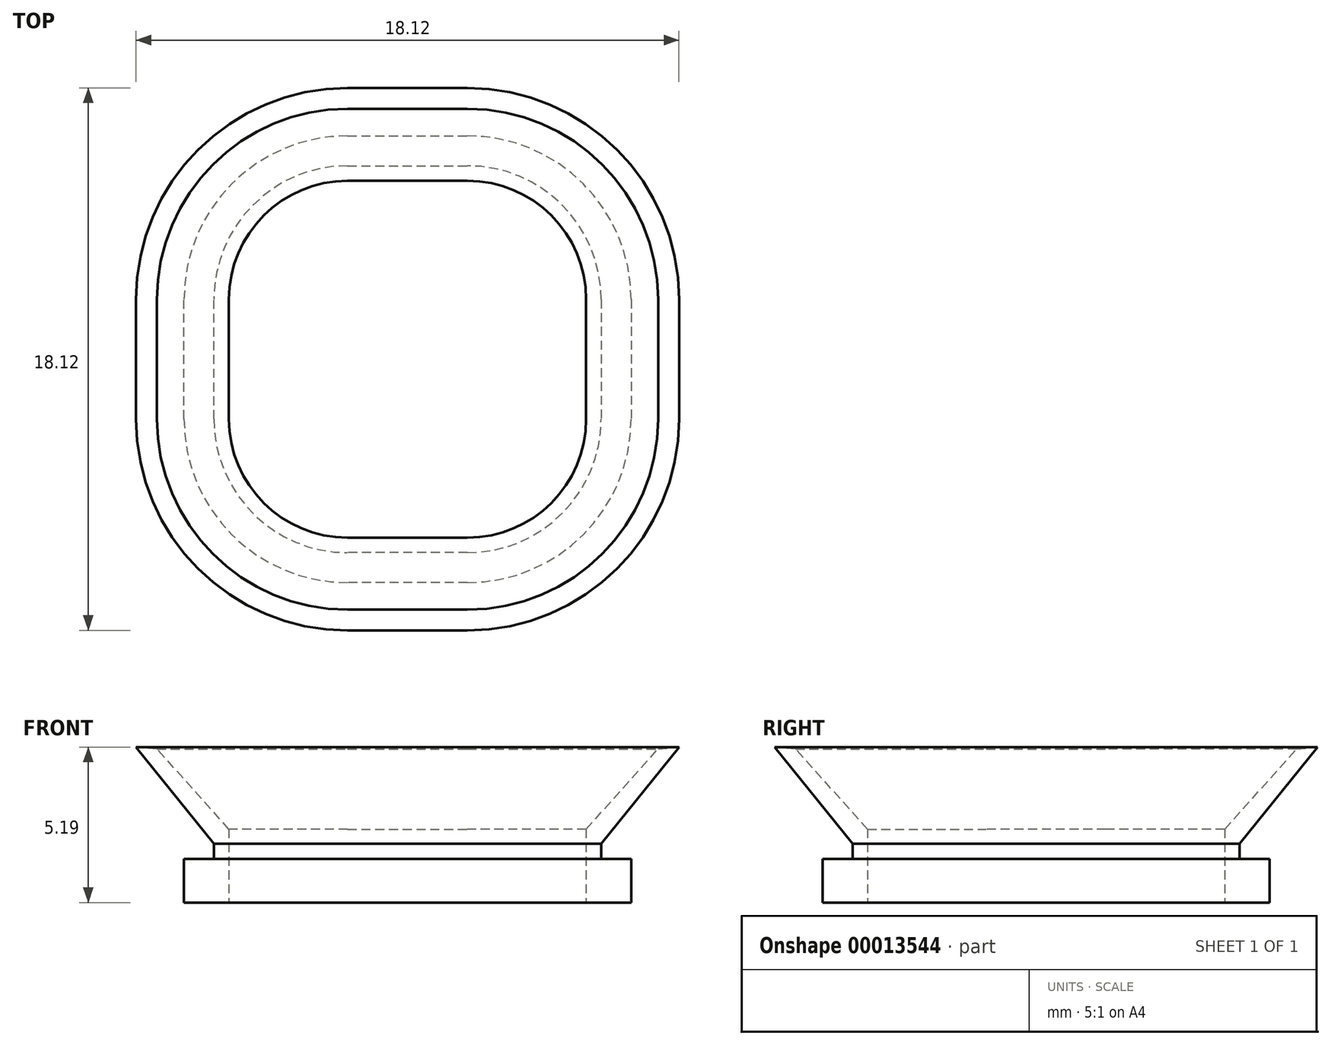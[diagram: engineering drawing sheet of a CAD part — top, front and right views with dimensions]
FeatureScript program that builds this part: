
annotation { "Feature Type Name" : "Feature", "Feature Type Description" : "" }
export const myFeature = defineFeature(function(context is Context, id is Id, definition is map)
    precondition{}
    {
        {
            var Q0;
            Q0=qCreatedBy(makeId("Top.planeOp"),FACE);
            var sketch = newSketch(context, id + "F0", { "sketchPlane" : qUnion([Q0])});
            skLineSegment(sketch, "E0.bottom", {"start": v(-143.48, -14.32) * mm, "end": v(-139.48, -14.32) * mm, "construction": true});
            skLineSegment(sketch, "E0.top", {"start": v(-143.48, -13.12) * mm, "end": v(-139.48, -13.12) * mm, "construction": true});
            skLineSegment(sketch, "E0.left", {"start": v(-143.48, -14.32) * mm, "end": v(-143.48, -13.12) * mm, "construction": true});
            skLineSegment(sketch, "E0.right", {"start": v(-139.48, -14.32) * mm, "end": v(-139.48, -13.12) * mm, "construction": true});
            skLineSegment(sketch, "E1", {"start": v(-143.48, -13.12) * mm, "end": v(-139.48, -13.12) * mm});
            skLineSegment(sketch, "E2", {"start": v(-143.48, -14.32) * mm, "end": v(-139.48, -14.32) * mm});
            skPoint(sketch, "E3", {"position": v(-141.48, -14.32) * mm});
            skLineSegment(sketch, "E4.1.0", {"start": v(-141.48, -23.84) * mm, "end": v(-141.48, -14.32) * mm, "construction": true});
            skPoint(sketch, "E4.2.2", {"position": v(-141.48, -23.84) * mm});
            skLineSegment(sketch, "E4.3.0", {"start": v(-141.48, -14.32) * mm, "end": v(-141.48, -23.84) * mm, "construction": true});
            skPoint(sketch, "E4.center", {"position": v(-141.48, -19.08) * mm});
            skLineSegment(sketch, "E5.1.0", {"start": v(-146.24, -21.08) * mm, "end": v(-146.24, -17.08) * mm});
            skLineSegment(sketch, "E5.1.1", {"start": v(-146.24, -17.08) * mm, "end": v(-147.44, -17.08) * mm, "construction": true});
            skLineSegment(sketch, "E5.1.2", {"start": v(-146.24, -21.08) * mm, "end": v(-147.44, -21.08) * mm, "construction": true});
            skPoint(sketch, "E5.1.3", {"position": v(-146.24, -19.08) * mm});
            skLineSegment(sketch, "E5.1.4", {"start": v(-147.44, -21.08) * mm, "end": v(-147.44, -17.08) * mm});
            skLineSegment(sketch, "E5.1.5", {"start": v(-146.24, -21.08) * mm, "end": v(-146.24, -17.08) * mm, "construction": true});
            skLineSegment(sketch, "E5.1.6", {"start": v(-147.44, -21.08) * mm, "end": v(-147.44, -17.08) * mm, "construction": true});
            skLineSegment(sketch, "E5.2.0", {"start": v(-139.48, -23.84) * mm, "end": v(-143.48, -23.84) * mm});
            skLineSegment(sketch, "E5.2.1", {"start": v(-143.48, -23.84) * mm, "end": v(-143.48, -25.04) * mm, "construction": true});
            skLineSegment(sketch, "E5.2.2", {"start": v(-139.48, -23.84) * mm, "end": v(-139.48, -25.04) * mm, "construction": true});
            skLineSegment(sketch, "E5.2.4", {"start": v(-139.48, -25.04) * mm, "end": v(-143.48, -25.04) * mm});
            skLineSegment(sketch, "E5.2.5", {"start": v(-139.48, -23.84) * mm, "end": v(-143.48, -23.84) * mm, "construction": true});
            skLineSegment(sketch, "E5.2.6", {"start": v(-139.48, -25.04) * mm, "end": v(-143.48, -25.04) * mm, "construction": true});
            skLineSegment(sketch, "E6.1.3.0", {"start": v(-136.72, -17.08) * mm, "end": v(-136.72, -21.08) * mm});
            skLineSegment(sketch, "E6.3.3.0", {"start": v(-136.72, -21.08) * mm, "end": v(-135.52, -21.08) * mm, "construction": true});
            skLineSegment(sketch, "E6.6.3.0", {"start": v(-136.72, -17.08) * mm, "end": v(-135.52, -17.08) * mm, "construction": true});
            skPoint(sketch, "E6.9.3.0", {"position": v(-136.72, -19.08) * mm});
            skLineSegment(sketch, "E6.10.3.0", {"start": v(-135.52, -17.08) * mm, "end": v(-135.52, -21.08) * mm});
            skLineSegment(sketch, "E6.13.3.0", {"start": v(-136.72, -17.08) * mm, "end": v(-136.72, -21.08) * mm, "construction": true});
            skLineSegment(sketch, "E6.16.3.0", {"start": v(-135.52, -17.08) * mm, "end": v(-135.52, -21.08) * mm, "construction": true});
            skArc(sketch, "E7", {"start": v(-143.48, -13.12) * mm, "mid": v(-146.28, -14.28) * mm, "end": v(-147.44, -17.08) * mm});
            skArc(sketch, "E8", {"start": v(-147.44, -21.08) * mm, "mid": v(-146.28, -23.88) * mm, "end": v(-143.48, -25.04) * mm});
            skArc(sketch, "E9", {"start": v(-135.52, -17.08) * mm, "mid": v(-136.68, -14.28) * mm, "end": v(-139.48, -13.12) * mm});
            skArc(sketch, "E10", {"start": v(-139.48, -25.04) * mm, "mid": v(-136.68, -23.88) * mm, "end": v(-135.52, -21.08) * mm});
            skLineSegment(sketch, "E11.0", {"start": v(-143.48, -11.62) * mm, "end": v(-139.48, -11.62) * mm});
            skArc(sketch, "E11.1", {"start": v(-134.02, -17.08) * mm, "mid": v(-135.62, -13.22) * mm, "end": v(-139.48, -11.62) * mm});
            skArc(sketch, "E11.2", {"start": v(-143.48, -11.62) * mm, "mid": v(-147.34, -13.22) * mm, "end": v(-148.94, -17.08) * mm});
            skLineSegment(sketch, "E11.3", {"start": v(-134.02, -17.08) * mm, "end": v(-134.02, -21.08) * mm});
            skLineSegment(sketch, "E11.4", {"start": v(-148.94, -21.08) * mm, "end": v(-148.94, -17.08) * mm});
            skArc(sketch, "E11.5", {"start": v(-148.94, -21.08) * mm, "mid": v(-147.34, -24.94) * mm, "end": v(-143.48, -26.54) * mm});
            skLineSegment(sketch, "E11.6", {"start": v(-139.48, -26.54) * mm, "end": v(-143.48, -26.54) * mm});
            skArc(sketch, "E11.7", {"start": v(-139.48, -26.54) * mm, "mid": v(-135.62, -24.94) * mm, "end": v(-134.02, -21.08) * mm});
            skSolve(sketch);
        }
        {
            var Q0;
            Q0 = qSketchRegion(id + "F0", true);
            extrude(context, id + "F1", {"entities" : qUnion([Q0]), "depth" : 2.45 * mm});
        }
        {
            var Q0;
            Q0=makeQuery(id+"F1.opExtrude","CAP_FACE",FACE,{"disambiguationData":[OSD([sQuery(id+"F0.wireOp",EDGE,"E1"),sQuery(id+"F0.wireOp",EDGE,"E5.1.4"),sQuery(id+"F0.wireOp",EDGE,"E5.2.4"),sQuery(id+"F0.wireOp",EDGE,"E6.10.3.0"),sQuery(id+"F0.wireOp",EDGE,"E7"),sQuery(id+"F0.wireOp",EDGE,"E8"),sQuery(id+"F0.wireOp",EDGE,"E9"),sQuery(id+"F0.wireOp",EDGE,"E10"),sQuery(id+"F0.wireOp",EDGE,"E11.0"),sQuery(id+"F0.wireOp",EDGE,"E11.1"),sQuery(id+"F0.wireOp",EDGE,"E11.2"),sQuery(id+"F0.wireOp",EDGE,"E11.3"),sQuery(id+"F0.wireOp",EDGE,"E11.4"),sQuery(id+"F0.wireOp",EDGE,"E11.5"),sQuery(id+"F0.wireOp",EDGE,"E11.6"),sQuery(id+"F0.wireOp",EDGE,"E11.7")])],"isStart":false});
            var sketch = newSketch(context, id + "F2", { "sketchPlane" : qUnion([Q0])});
            skLineSegment(sketch, "E12", {"start": v(-143.48, -12.62) * mm, "end": v(-139.48, -12.62) * mm});
            skArc(sketch, "E13", {"start": v(-143.48, -12.62) * mm, "mid": v(-146.63, -13.92) * mm, "end": v(-147.94, -17.08) * mm});
            skLineSegment(sketch, "E14", {"start": v(-147.44, -19.08) * mm, "end": v(-135.52, -19.08) * mm, "construction": true});
            skArc(sketch, "E15.1.0", {"start": v(-147.94, -21.08) * mm, "mid": v(-146.63, -24.24) * mm, "end": v(-143.48, -25.54) * mm});
            skLineSegment(sketch, "E15.1.1", {"start": v(-147.94, -21.08) * mm, "end": v(-147.94, -17.08) * mm});
            skPoint(sketch, "E15.center", {"position": v(-141.48, -19.08) * mm});
            skArc(sketch, "E16.3.2.0", {"start": v(-139.48, -25.54) * mm, "mid": v(-136.32, -24.24) * mm, "end": v(-135.02, -21.08) * mm});
            skLineSegment(sketch, "E16.4.2.0", {"start": v(-139.48, -25.54) * mm, "end": v(-143.48, -25.54) * mm});
            skArc(sketch, "E16.3.3.0", {"start": v(-135.02, -17.08) * mm, "mid": v(-136.32, -13.92) * mm, "end": v(-139.48, -12.62) * mm});
            skLineSegment(sketch, "E16.4.3.0", {"start": v(-135.02, -17.08) * mm, "end": v(-135.02, -21.08) * mm});
            skArc(sketch, "E17.0", {"start": v(-143.48, -11.62) * mm, "mid": v(-147.34, -13.22) * mm, "end": v(-148.94, -17.08) * mm});
            skLineSegment(sketch, "E17.1", {"start": v(-148.94, -21.08) * mm, "end": v(-148.94, -17.08) * mm});
            skLineSegment(sketch, "E17.2", {"start": v(-143.48, -11.62) * mm, "end": v(-139.48, -11.62) * mm});
            skArc(sketch, "E17.3", {"start": v(-148.94, -21.08) * mm, "mid": v(-147.34, -24.94) * mm, "end": v(-143.48, -26.54) * mm});
            skArc(sketch, "E17.4", {"start": v(-134.02, -17.08) * mm, "mid": v(-135.62, -13.22) * mm, "end": v(-139.48, -11.62) * mm});
            skLineSegment(sketch, "E17.5", {"start": v(-134.02, -17.08) * mm, "end": v(-134.02, -21.08) * mm});
            skArc(sketch, "E17.6", {"start": v(-139.48, -26.54) * mm, "mid": v(-135.62, -24.94) * mm, "end": v(-134.02, -21.08) * mm});
            skLineSegment(sketch, "E17.7", {"start": v(-139.48, -26.54) * mm, "end": v(-143.48, -26.54) * mm});
            skSolve(sketch);
        }
        {
            var Q0;
            Q0 = qSketchRegion(id + "F2", true);
            extrude(context, id + "F3", {"entities" : qUnion([Q0]), "operationType" : NewBodyOperationType.REMOVE, "oppositeDirection" : true, "depth" : 1 * mm});
        }
        {
            var Q0;
            Q0=makeQuery(id+"F1.opExtrude","CAP_VERTEX",VERTEX,{"disambiguationData":[OSD([sQuery(id+"F0.wireOp",EDGE,"E5.1.4"),sQuery(id+"F0.wireOp",EDGE,"E7")])],"isStart":false});
            var Q1;
            Q1=makeQuery(id+"F1.opExtrude","CAP_VERTEX",VERTEX,{"disambiguationData":[OSD([sQuery(id+"F0.wireOp",EDGE,"E5.1.4"),sQuery(id+"F0.wireOp",EDGE,"E7")])],"isStart":true});
            var Q2;
            Q2=makeQuery(id+"F1.opExtrude","CAP_VERTEX",VERTEX,{"disambiguationData":[OSD([sQuery(id+"F0.wireOp",EDGE,"E6.10.3.0"),sQuery(id+"F0.wireOp",EDGE,"E9")])],"isStart":false});
            cPlane(context, id + "F4", {"entities" : qUnion([Q0, Q1, Q2]), "cplaneType" : CPlaneType.THREE_POINT, "offset" : 150 * mm, "width" : 150 * mm, "height" : 150 * mm});
        }
        {
            var Q0;
            Q0=qCreatedBy(id+"F4.planeOp",FACE);
            var sketch = newSketch(context, id + "F5", { "sketchPlane" : qUnion([Q0])});
            skLineSegment(sketch, "E18", {"start": v(135.52, 2.45) * mm, "end": v(133.11, 5.13) * mm});
            skLineSegment(sketch, "E19", {"start": v(133.11, 5.13) * mm, "end": v(132.42, 5.2) * mm});
            skLineSegment(sketch, "E20", {"start": v(132.42, 5.2) * mm, "end": v(135.02, 1.96) * mm});
            skLineSegment(sketch, "E21", {"start": v(135.02, 1.96) * mm, "end": v(135.52, 2.45) * mm});
            skSolve(sketch);
        }
        {
            var Q0;
            Q0 = qSketchRegion(id + "F5", true);
            var Q1;
            Q1=makeQuery(id+"F1.opExtrude","CAP_EDGE",EDGE,{"disambiguationData":[OSD([sQuery(id+"F0.wireOp",EDGE,"E6.10.3.0")])],"isStart":false});
            var Q2;
            Q2=makeQuery(id+"F1.opExtrude","CAP_EDGE",EDGE,{"disambiguationData":[OSD([sQuery(id+"F0.wireOp",EDGE,"E10")])],"isStart":false});
            var Q3;
            Q3=makeQuery(id+"F1.opExtrude","CAP_EDGE",EDGE,{"disambiguationData":[OSD([sQuery(id+"F0.wireOp",EDGE,"E5.2.4")])],"isStart":false});
            var Q4;
            Q4=makeQuery(id+"F1.opExtrude","CAP_EDGE",EDGE,{"disambiguationData":[OSD([sQuery(id+"F0.wireOp",EDGE,"E8")])],"isStart":false});
            var Q5;
            Q5=makeQuery(id+"F1.opExtrude","CAP_EDGE",EDGE,{"disambiguationData":[OSD([sQuery(id+"F0.wireOp",EDGE,"E5.1.4")])],"isStart":false});
            var Q6;
            Q6=makeQuery(id+"F1.opExtrude","CAP_EDGE",EDGE,{"disambiguationData":[OSD([sQuery(id+"F0.wireOp",EDGE,"E7")])],"isStart":false});
            var Q7;
            Q7=makeQuery(id+"F1.opExtrude","CAP_EDGE",EDGE,{"disambiguationData":[OSD([sQuery(id+"F0.wireOp",EDGE,"E1")])],"isStart":false});
            var Q8;
            Q8=makeQuery(id+"F1.opExtrude","CAP_EDGE",EDGE,{"disambiguationData":[OSD([sQuery(id+"F0.wireOp",EDGE,"E9")])],"isStart":false});
            sweep(context, id + "F6", {"operationType" : NewBodyOperationType.ADD, "profiles" : qUnion([Q0]), "path" : qUnion([Q1, Q2, Q3, Q4, Q5, Q6, Q7, Q8])});
        }
    });
